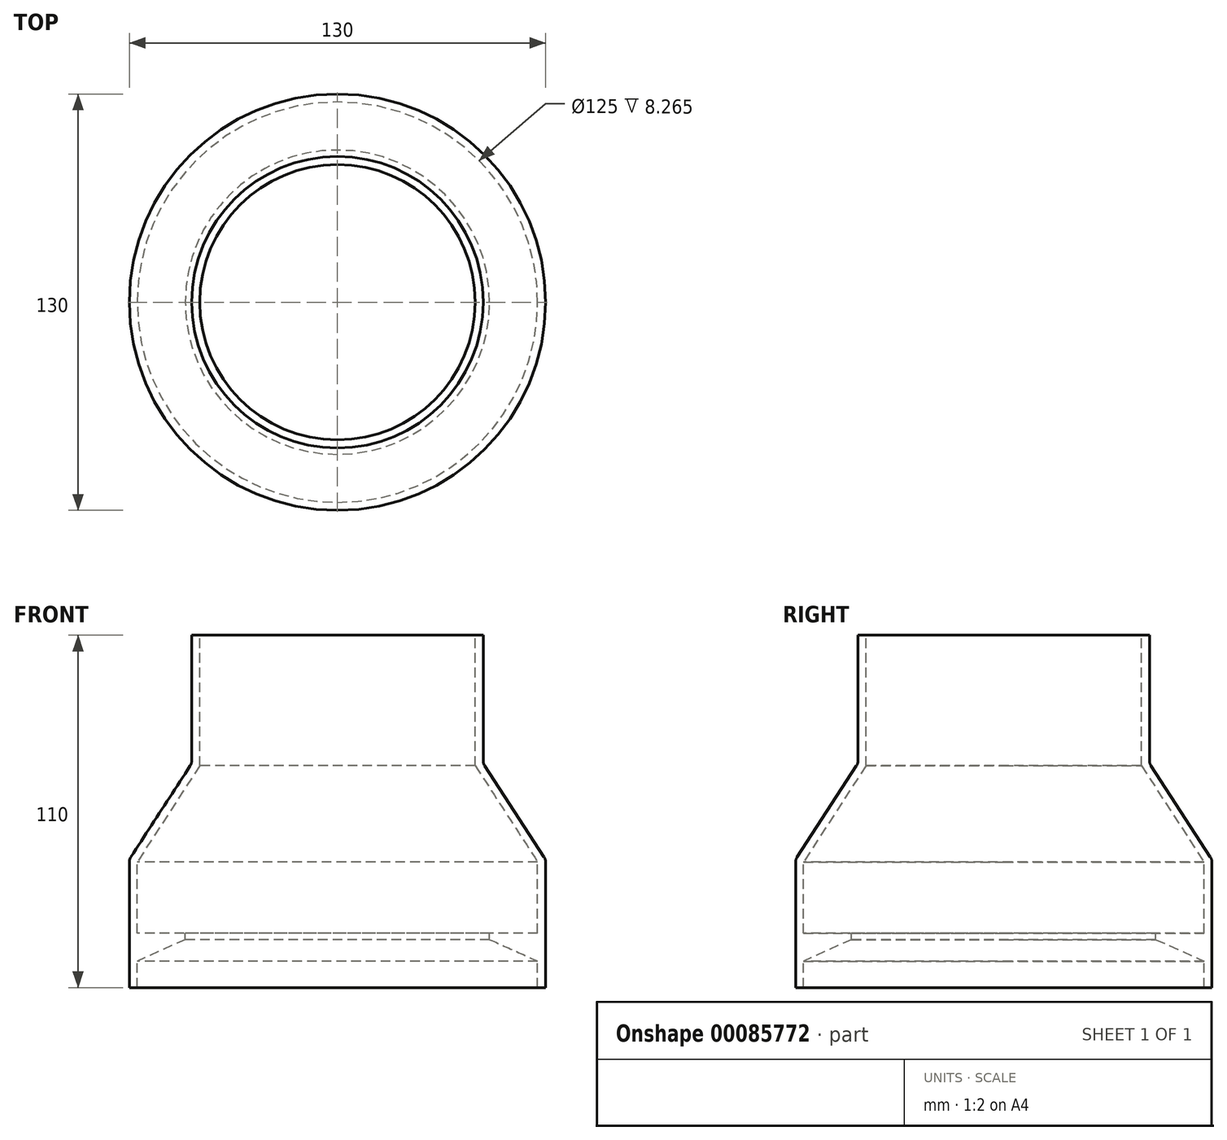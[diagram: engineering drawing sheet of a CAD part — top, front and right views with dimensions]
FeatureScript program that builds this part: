
annotation { "Feature Type Name" : "Feature", "Feature Type Description" : "" }
export const myFeature = defineFeature(function(context is Context, id is Id, definition is map)
    precondition{}
    {
        {
            var Q0;
            Q0=qCreatedBy(makeId("Front.planeOp"),FACE);
            var sketch = newSketch(context, id + "F0", { "sketchPlane" : qUnion([Q0])});
            skLineSegment(sketch, "E0", {"start": v(0, 120.15) * mm, "end": v(0, -114.03) * mm, "construction": true});
            skLineSegment(sketch, "E1", {"start": v(45.5, 56.89) * mm, "end": v(45.5, 16.89) * mm});
            skLineSegment(sketch, "E2", {"start": v(45.5, 16.89) * mm, "end": v(65, -13.11) * mm});
            skLineSegment(sketch, "E3", {"start": v(65, -13.11) * mm, "end": v(65, -53.11) * mm});
            skLineSegment(sketch, "E4.0", {"start": v(62.5, -13.85) * mm, "end": v(62.5, -36.11) * mm});
            skLineSegment(sketch, "E4.1", {"start": v(43, 16.15) * mm, "end": v(62.5, -13.85) * mm});
            skLineSegment(sketch, "E4.2", {"start": v(43, 56.89) * mm, "end": v(43, 16.15) * mm});
            skLineSegment(sketch, "E5", {"start": v(43, 56.89) * mm, "end": v(45.5, 56.89) * mm});
            skLineSegment(sketch, "E6", {"start": v(62.5, -53.11) * mm, "end": v(65, -53.11) * mm});
            skLineSegment(sketch, "E7", {"start": v(47.5, -38.11) * mm, "end": v(47.5, -36.11) * mm});
            skLineSegment(sketch, "E8", {"start": v(47.5, -36.11) * mm, "end": v(62.5, -36.11) * mm});
            skLineSegment(sketch, "E9.trimOffspring", {"start": v(62.5, -44.85) * mm, "end": v(62.5, -53.11) * mm});
            skLineSegment(sketch, "E10", {"start": v(47.5, -38.11) * mm, "end": v(62.5, -44.85) * mm});
            skSolve(sketch);
        }
        {
            var Q0;
            Q0 = qSketchRegion(id + "F0", true);
            var Q1;
            Q1=sQuery(id+"F0.wireOp",EDGE,"E0");
            revolve(context, id + "F1", {"entities" : qUnion([Q0]), "axis" : qUnion([Q1]), "revolveType" : RevolveType.FULL});
        }
        {
            var Q0;
            Q0=makeQuery(id+"F1.opRevolve","SWEPT_EDGE",EDGE,{"disambiguationData":[OSD([sQuery(id+"F0.wireOp",EDGE,"E2"),sQuery(id+"F0.wireOp",EDGE,"E3")])]});
            var Q1;
            Q1=makeQuery(id+"F1.opRevolve","SWEPT_EDGE",EDGE,{"disambiguationData":[OSD([sQuery(id+"F0.wireOp",EDGE,"E1"),sQuery(id+"F0.wireOp",EDGE,"E2")])]});
            fillet(context, id + "F2", {"entities" : qUnion([Q0, Q1]), "radius" : 3 * mm, "tangentPropagation" : true, "allowEdgeOverflow" : false});
        }
    });
